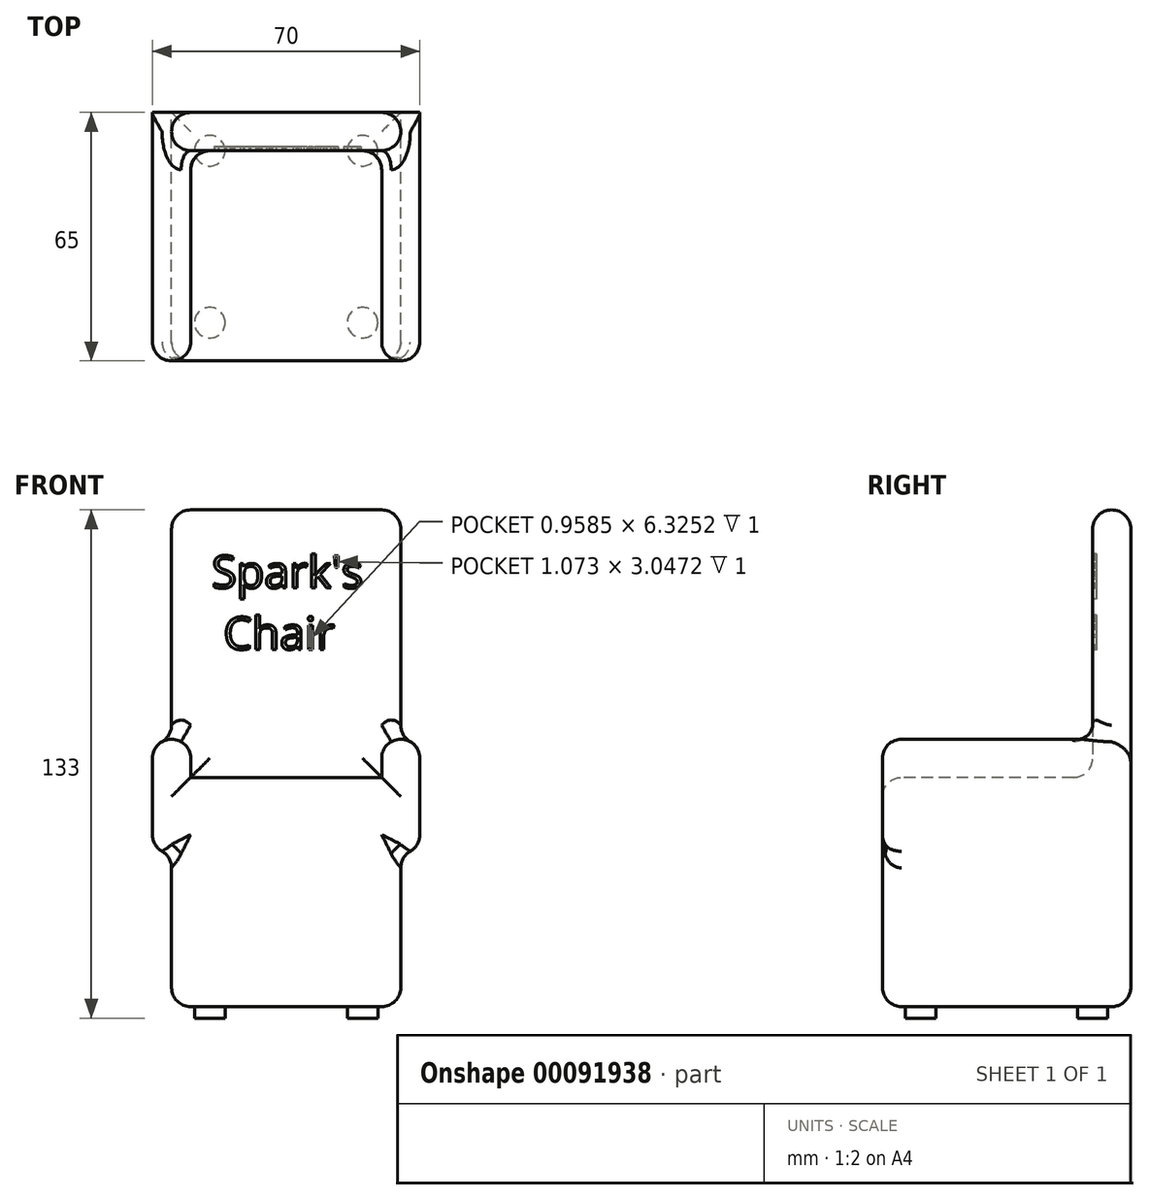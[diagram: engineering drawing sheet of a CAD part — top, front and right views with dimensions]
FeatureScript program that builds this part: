
annotation { "Feature Type Name" : "Feature", "Feature Type Description" : "" }
export const myFeature = defineFeature(function(context is Context, id is Id, definition is map)
    precondition{}
    {
        {
            var Q0;
            Q0=qCreatedBy(makeId("Top.planeOp"),FACE);
            var sketch = newSketch(context, id + "F0", { "sketchPlane" : qUnion([Q0])});
            skLineSegment(sketch, "E0.bottom", {"start": v(0, 0) * mm, "end": v(60, 0) * mm});
            skLineSegment(sketch, "E0.top", {"start": v(0, 65) * mm, "end": v(60, 65) * mm});
            skLineSegment(sketch, "E0.left", {"start": v(0, 0) * mm, "end": v(0, 65) * mm});
            skLineSegment(sketch, "E0.right", {"start": v(60, 0) * mm, "end": v(60, 65) * mm});
            skLineSegment(sketch, "E1", {"start": v(0, 55) * mm, "end": v(60, 55) * mm});
            skSolve(sketch);
        }
        {
            var Q0;
            Q0=makeQuery(id+"F0.imprint","IMPRINT",FACE,{"disambiguationData":[TD([[makeQuery(id+"F0.imprint","IMPRINT",EDGE,{"derivedFrom":sQuery(id+"F0.wireOp",EDGE,"E0.bottom")}),1.0]])]});
            extrude(context, id + "F1", {"entities" : qUnion([Q0]), "depth" : 60 * mm});
        }
        {
            var Q0;
            {var subQ0=sQuery(id+"F0.wireOp",EDGE,"E0.top");Q0=makeQuery(id+"F0.imprint","IMPRINT",FACE,{"disambiguationData":[TD([[makeQuery(id+"F0.imprint","IMPRINT",EDGE,{"derivedFrom":subQ0}),-1.0]])]});}
            extrude(context, id + "F2", {"entities" : qUnion([Q0]), "operationType" : NewBodyOperationType.ADD, "depth" : 130 * mm});
        }
        {
            var Q0;
            Q0=makeQuery(id+"F1.opExtrude","SWEPT_FACE",FACE,{"disambiguationData":[OSD([sQuery(id+"F0.wireOp",EDGE,"E0.bottom")])]});
            var sketch = newSketch(context, id + "F3", { "sketchPlane" : qUnion([Q0])});
            skLineSegment(sketch, "E2.bottom", {"start": v(-5, 70) * mm, "end": v(5, 70) * mm});
            skLineSegment(sketch, "E2.top", {"start": v(-5, 40) * mm, "end": v(5, 40) * mm});
            skLineSegment(sketch, "E2.left", {"start": v(-5, 70) * mm, "end": v(-5, 40) * mm});
            skLineSegment(sketch, "E2.right", {"start": v(5, 70) * mm, "end": v(5, 40) * mm});
            skLineSegment(sketch, "E3.bottom", {"start": v(55, 70) * mm, "end": v(65, 70) * mm});
            skLineSegment(sketch, "E3.top", {"start": v(55, 40) * mm, "end": v(65, 40) * mm});
            skLineSegment(sketch, "E3.left", {"start": v(55, 70) * mm, "end": v(55, 40) * mm});
            skLineSegment(sketch, "E3.right", {"start": v(65, 70) * mm, "end": v(65, 40) * mm});
            skSolve(sketch);
        }
        {
            var Q0;
            {var subQ6=sQuery(id+"F3.wireOp",EDGE,"E2.bottom");Q0=makeQuery(id+"F3.imprint","IMPRINT",FACE,{"disambiguationData":[TD([[makeQuery(id+"F3.imprint","IMPRINT",EDGE,{"derivedFrom":subQ6}),-1.0]])]});}
            var Q1;
            {var subQ2=sQuery(id+"F3.wireOp",EDGE,"E3.bottom");Q1=makeQuery(id+"F3.imprint","IMPRINT",FACE,{"disambiguationData":[TD([[makeQuery(id+"F3.imprint","IMPRINT",EDGE,{"derivedFrom":subQ2}),-1.0]])]});}
            var Q2;
            Q2=makeQuery(id+"F2.opExtrude","SWEPT_FACE",FACE,{"disambiguationData":[OSD([sQuery(id+"F0.wireOp",EDGE,"E0.top")])]});
            extrude(context, id + "F4", {"entities" : qUnion([Q0, Q1]), "operationType" : NewBodyOperationType.ADD, "endBound" : BoundingType.UP_TO_SURFACE, "oppositeDirection" : true, "endBoundEntityFace" : qUnion([Q2]), "depth" : 45.8 * mm});
        }
        {
            var Q0;
            Q0=makeQuery(id+"F4.opExtrude","SWEPT_EDGE",EDGE,{"disambiguationData":[OSD([sQuery(id+"F3.wireOp",EDGE,"E2.top"),sQuery(id+"F3.wireOp",EDGE,"E2.left")])]});
            var Q1;
            Q1=makeQuery(id+"F4.opExtrude","SWEPT_EDGE",EDGE,{"disambiguationData":[OSD([sQuery(id+"F3.wireOp",EDGE,"E2.bottom"),sQuery(id+"F3.wireOp",EDGE,"E2.left")])]});
            var Q2;
            Q2=makeQuery(id+"F4.opExtrude","SWEPT_EDGE",EDGE,{"disambiguationData":[OSD([sQuery(id+"F3.wireOp",EDGE,"E2.bottom"),sQuery(id+"F3.wireOp",EDGE,"E2.right")])]});
            var Q3;
            Q3=makeQuery(id+"F4.opExtrude","SWEPT_EDGE",EDGE,{"disambiguationData":[OSD([sQuery(id+"F3.wireOp",EDGE,"E3.bottom"),sQuery(id+"F3.wireOp",EDGE,"E3.left")])]});
            var Q4;
            Q4=makeQuery(id+"F4.opExtrude","SWEPT_EDGE",EDGE,{"disambiguationData":[OSD([sQuery(id+"F3.wireOp",EDGE,"E3.bottom"),sQuery(id+"F3.wireOp",EDGE,"E3.right")])]});
            var Q5;
            Q5=makeQuery(id+"F4.opExtrude","SWEPT_EDGE",EDGE,{"disambiguationData":[OSD([sQuery(id+"F3.wireOp",EDGE,"E3.top"),sQuery(id+"F3.wireOp",EDGE,"E3.right")])]});
            var Q6;
            {var subQ0=sQuery(id+"F0.wireOp",EDGE,"E0.bottom");Q6=makeQuery(id+"F4.boolean.opBoolean","MERGE",FACE,{"derivedFrom":[makeQuery(id+"F1.opExtrude","SWEPT_FACE",FACE,{"disambiguationData":[OSD([subQ0])]}),makeQuery(id+"F4.opExtrude","CAP_FACE",FACE,{"disambiguationData":[OSD([subQ0,sQuery(id+"F0.wireOp",EDGE,"E0.left"),sQuery(id+"F3.wireOp",EDGE,"E2.bottom"),sQuery(id+"F3.wireOp",EDGE,"E2.top"),sQuery(id+"F3.wireOp",EDGE,"E2.left"),sQuery(id+"F3.wireOp",EDGE,"E2.right")])],"isStart":true}),makeQuery(id+"F4.opExtrude","CAP_FACE",FACE,{"disambiguationData":[OSD([subQ0,sQuery(id+"F0.wireOp",EDGE,"E0.right"),sQuery(id+"F3.wireOp",EDGE,"E3.bottom"),sQuery(id+"F3.wireOp",EDGE,"E3.top"),sQuery(id+"F3.wireOp",EDGE,"E3.left"),sQuery(id+"F3.wireOp",EDGE,"E3.right")])],"isStart":true})]});}
            var Q7;
            {var subQ0=sQuery(id+"F0.wireOp",EDGE,"E0.left");Q7=makeQuery(id+"F2.boolean.opBoolean","MERGE",EDGE,{"derivedFrom":[makeQuery(id+"F1.opExtrude","CAP_EDGE",EDGE,{"disambiguationData":[OSD([subQ0])],"isStart":true}),makeQuery(id+"F2.opExtrude","CAP_EDGE",EDGE,{"disambiguationData":[OSD([subQ0])],"isStart":true})]});}
            var Q8;
            {var subQ0=sQuery(id+"F0.wireOp",EDGE,"E0.right");Q8=makeQuery(id+"F2.boolean.opBoolean","MERGE",EDGE,{"derivedFrom":[makeQuery(id+"F1.opExtrude","CAP_EDGE",EDGE,{"disambiguationData":[OSD([subQ0])],"isStart":true}),makeQuery(id+"F2.opExtrude","CAP_EDGE",EDGE,{"disambiguationData":[OSD([subQ0])],"isStart":true})]});}
            var Q9;
            Q9=makeQuery(id+"F2.opExtrude","CAP_EDGE",EDGE,{"disambiguationData":[OSD([sQuery(id+"F0.wireOp",EDGE,"E0.top")])],"isStart":true});
            fillet(context, id + "F5", {"entities" : qUnion([Q0, Q1, Q2, Q3, Q4, Q5, Q6, Q7, Q8, Q9]), "radius" : 5 * mm, "tangentPropagation" : true, "allowEdgeOverflow" : false});
        }
        {
            var Q0;
            Q0=makeQuery(id+"F2.opExtrude","CAP_FACE",FACE,{"disambiguationData":[OSD([sQuery(id+"F0.wireOp",EDGE,"E0.top"),sQuery(id+"F0.wireOp",EDGE,"E0.left"),sQuery(id+"F0.wireOp",EDGE,"E0.right"),sQuery(id+"F0.wireOp",EDGE,"E1")])],"isStart":false});
            var Q1;
            {var subQ1=sQuery(id+"F0.wireOp",EDGE,"E1");var subQ2=sQuery(id+"F0.wireOp",EDGE,"E0.right");Q1=makeQuery(id+"F4.boolean.opBoolean","SPLIT",FACE,{"disambiguationData":[TD([makeQuery(id+"F2.opExtrude","SWEPT_FACE",FACE,{"disambiguationData":[OSD([subQ1])]})])],"derivedFrom":makeQuery(id+"F2.boolean.opBoolean","MERGE",FACE,{"derivedFrom":[makeQuery(id+"F1.opExtrude","SWEPT_FACE",FACE,{"disambiguationData":[OSD([subQ2])]}),makeQuery(id+"F2.opExtrude","SWEPT_FACE",FACE,{"disambiguationData":[OSD([subQ2])]})]})});}
            var Q2;
            Q2=makeQuery(id+"F2.opExtrude","SWEPT_FACE",FACE,{"disambiguationData":[OSD([sQuery(id+"F0.wireOp",EDGE,"E1")])]});
            var Q3;
            {var subQ1=sQuery(id+"F0.wireOp",EDGE,"E1");var subQ5=sQuery(id+"F0.wireOp",EDGE,"E0.left");Q3=makeQuery(id+"F4.boolean.opBoolean","SPLIT",FACE,{"disambiguationData":[TD([makeQuery(id+"F2.opExtrude","SWEPT_FACE",FACE,{"disambiguationData":[OSD([subQ1])]})])],"derivedFrom":makeQuery(id+"F2.boolean.opBoolean","MERGE",FACE,{"derivedFrom":[makeQuery(id+"F1.opExtrude","SWEPT_FACE",FACE,{"disambiguationData":[OSD([subQ5])]}),makeQuery(id+"F2.opExtrude","SWEPT_FACE",FACE,{"disambiguationData":[OSD([subQ5])]})]})});}
            fillet(context, id + "F6", {"entities" : qUnion([Q0, Q1, Q2, Q3]), "radius" : 5 * mm, "tangentPropagation" : true, "allowEdgeOverflow" : false});
        }
        {
            var Q0;
            Q0=makeQuery(id+"F2.opExtrude","SWEPT_FACE",FACE,{"disambiguationData":[OSD([sQuery(id+"F0.wireOp",EDGE,"E1")])]});
            var sketch = newSketch(context, id + "F7", { "sketchPlane" : qUnion([Q0])});
            skText(sketch, "E4", { "text": "Spark\'s\n Chair", "fontName": "OpenSans-Regular.ttf"});
            const initialGuessF7  = {"E4": [0.01052, 0.10957, 1, 0, 0.00851]};
            skSetInitialGuess(sketch, initialGuessF7);
            skSolve(sketch);
        }
        {
            var Q0;
            Q0 = qSketchRegion(id + "F7", true);
            extrude(context, id + "F8", {"entities" : qUnion([Q0]), "operationType" : NewBodyOperationType.REMOVE, "oppositeDirection" : true, "depth" : 1 * mm});
        }
        {
            var Q0;
            {var subQ0=sQuery(id+"F0.wireOp",EDGE,"E0.bottom");Q0=makeQuery(id+"F0.imprint","IMPRINT",FACE,{"disambiguationData":[TD([[makeQuery(id+"F0.imprint","IMPRINT",EDGE,{"derivedFrom":subQ0}),1.0]])]});}
            var sketch = newSketch(context, id + "F9", { "sketchPlane" : qUnion([Q0])});
            skCircle(sketch, "E5", {"center": v(10, 10) * mm, "radius": 4 * mm});
            skCircle(sketch, "E6", {"center": v(50, 10) * mm, "radius": 4 * mm});
            skCircle(sketch, "E7", {"center": v(50, 55) * mm, "radius": 4 * mm});
            skCircle(sketch, "E8", {"center": v(10, 55) * mm, "radius": 4 * mm});
            skSolve(sketch);
        }
        {
            var Q0;
            Q0 = qSketchRegion(id + "F9", true);
            extrude(context, id + "F10", {"entities" : qUnion([Q0]), "operationType" : NewBodyOperationType.ADD, "oppositeDirection" : true, "depth" : 3 * mm});
        }
        {
            var Q0;
            {var subQ2=sQuery(id+"F0.wireOp",EDGE,"E0.left");var subQ8=sQuery(id+"F0.wireOp",EDGE,"E0.bottom");var subQ10=sQuery(id+"F3.wireOp",EDGE,"E2.left");var subQ11=sQuery(id+"F3.wireOp",EDGE,"E2.top");Q0=makeQuery(id+"F5.opFillet","BLEND_EDGE",EDGE,{"blendedFrom":[makeQuery(id+"F4.opExtrude","SWEPT_EDGE",EDGE,{"disambiguationData":[OSD([subQ11,subQ10])]}),makeQuery(id+"F4.boolean.opBoolean","SPLIT",FACE,{"disambiguationData":[TD([makeQuery(id+"F1.opExtrude","SWEPT_FACE",FACE,{"disambiguationData":[OSD([subQ8])]})])],"derivedFrom":makeQuery(id+"F2.boolean.opBoolean","MERGE",FACE,{"derivedFrom":[makeQuery(id+"F1.opExtrude","SWEPT_FACE",FACE,{"disambiguationData":[OSD([subQ2])]}),makeQuery(id+"F2.opExtrude","SWEPT_FACE",FACE,{"disambiguationData":[OSD([subQ2])]})]})})],"blendedInto":[makeQuery(id+"F4.boolean.opBoolean","SPLIT",FACE,{"disambiguationData":[TD([makeQuery(id+"F1.opExtrude","SWEPT_FACE",FACE,{"disambiguationData":[OSD([subQ8])]})])],"derivedFrom":makeQuery(id+"F2.boolean.opBoolean","MERGE",FACE,{"derivedFrom":[makeQuery(id+"F1.opExtrude","SWEPT_FACE",FACE,{"disambiguationData":[OSD([subQ2])]}),makeQuery(id+"F2.opExtrude","SWEPT_FACE",FACE,{"disambiguationData":[OSD([subQ2])]})]})})]});}
            var Q1;
            {var subQ1=sQuery(id+"F0.wireOp",EDGE,"E0.right");var subQ4=sQuery(id+"F3.wireOp",EDGE,"E3.right");var subQ6=sQuery(id+"F3.wireOp",EDGE,"E3.top");var subQ8=sQuery(id+"F0.wireOp",EDGE,"E0.bottom");Q1=makeQuery(id+"F5.opFillet","BLEND_EDGE",EDGE,{"blendedFrom":[makeQuery(id+"F4.opExtrude","SWEPT_EDGE",EDGE,{"disambiguationData":[OSD([subQ6,subQ4])]}),makeQuery(id+"F4.boolean.opBoolean","SPLIT",FACE,{"disambiguationData":[TD([makeQuery(id+"F1.opExtrude","SWEPT_FACE",FACE,{"disambiguationData":[OSD([subQ8])]})])],"derivedFrom":makeQuery(id+"F2.boolean.opBoolean","MERGE",FACE,{"derivedFrom":[makeQuery(id+"F1.opExtrude","SWEPT_FACE",FACE,{"disambiguationData":[OSD([subQ1])]}),makeQuery(id+"F2.opExtrude","SWEPT_FACE",FACE,{"disambiguationData":[OSD([subQ1])]})]})})],"blendedInto":[makeQuery(id+"F4.boolean.opBoolean","SPLIT",FACE,{"disambiguationData":[TD([makeQuery(id+"F1.opExtrude","SWEPT_FACE",FACE,{"disambiguationData":[OSD([subQ8])]})])],"derivedFrom":makeQuery(id+"F2.boolean.opBoolean","MERGE",FACE,{"derivedFrom":[makeQuery(id+"F1.opExtrude","SWEPT_FACE",FACE,{"disambiguationData":[OSD([subQ1])]}),makeQuery(id+"F2.opExtrude","SWEPT_FACE",FACE,{"disambiguationData":[OSD([subQ1])]})]})})]});}
            fillet(context, id + "F11", {"entities" : qUnion([Q0, Q1]), "radius" : 5 * mm, "tangentPropagation" : true, "allowEdgeOverflow" : false});
        }
    });
